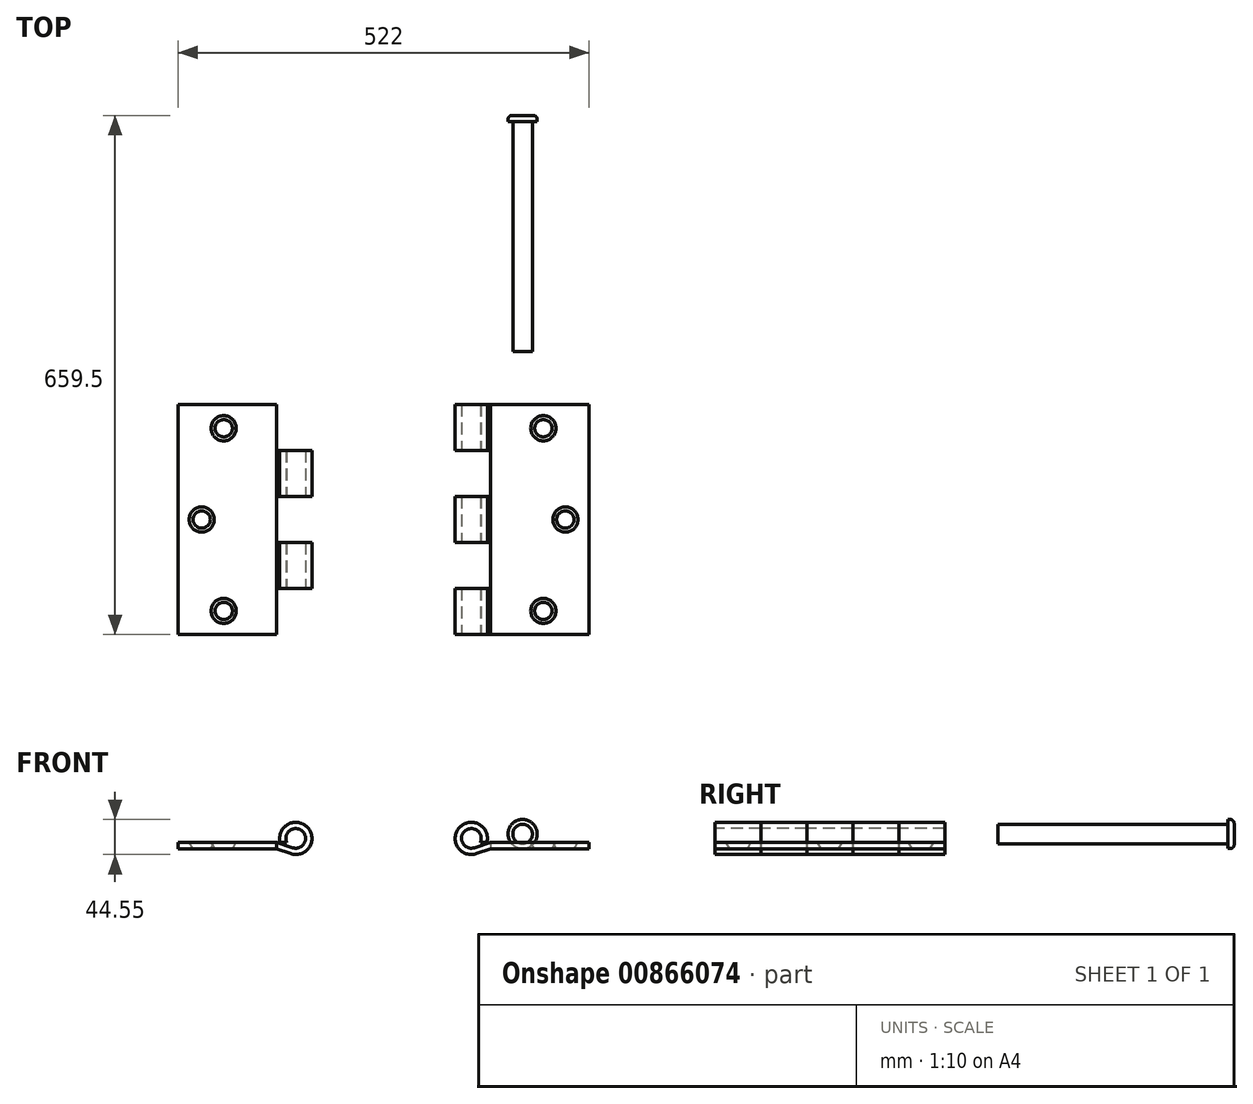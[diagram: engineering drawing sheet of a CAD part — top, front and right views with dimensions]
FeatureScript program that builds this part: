
annotation { "Feature Type Name" : "Feature", "Feature Type Description" : "" }
export const myFeature = defineFeature(function(context is Context, id is Id, definition is map)
    precondition{}
    {
        {
            var Q0;
            Q0=qCreatedBy(makeId("Top.planeOp"),FACE);
            var sketch = newSketch(context, id + "F0", { "sketchPlane" : qUnion([Q0])});
            skLineSegment(sketch, "E0.bottom", {"start": v(-62.5, 146) * mm, "end": v(62.5, 146) * mm});
            skLineSegment(sketch, "E0.top", {"start": v(-62.5, -146) * mm, "end": v(62.5, -146) * mm});
            skLineSegment(sketch, "E0.left", {"start": v(-62.5, 146) * mm, "end": v(-62.5, -146) * mm});
            skLineSegment(sketch, "E0.right", {"start": v(62.5, 146) * mm, "end": v(62.5, -146) * mm});
            skPoint(sketch, "E0.middle", {"position": v(0, 0) * mm});
            skSolve(sketch);
        }
        {
            var Q0;
            Q0=makeQuery(id+"F0.imprint","IMPRINT",FACE,{"disambiguationData":[TD([[makeQuery(id+"F0.imprint","IMPRINT",EDGE,{"derivedFrom":sQuery(id+"F0.wireOp",EDGE,"E0.bottom")}),-1.0]])]});
            extrude(context, id + "F1", {"entities" : qUnion([Q0]), "depth" : 8 * mm, "offsetDistance" : 25 * mm});
        }
        {
            var Q0;
            Q0=makeQuery(id+"F1.opExtrude","SWEPT_FACE",FACE,{"disambiguationData":[OSD([sQuery(id+"F0.wireOp",EDGE,"E0.top")])]});
            var sketch = newSketch(context, id + "F2", { "sketchPlane" : qUnion([Q0])});
            skArc(sketch, "E1", {"start": v(-67.12, 8) * mm, "mid": v(-102.19, 26.77) * mm, "end": v(-80.09, -6.3) * mm});
            skArc(sketch, "E2", {"start": v(-75.54, 8) * mm, "mid": v(-95.44, 22.22) * mm, "end": v(-83.04, 1.14) * mm});
            skLineSegment(sketch, "E3", {"start": v(-67.12, 8) * mm, "end": v(-75.54, 8) * mm});
            skLineSegment(sketch, "E4", {"start": v(-62.5, 0) * mm, "end": v(-80.09, -6.3) * mm});
            skLineSegment(sketch, "E5", {"start": v(-62.5, 8) * mm, "end": v(-83.04, 1.14) * mm});
            skSolve(sketch);
        }
        {
            var Q0;
            Q0=makeQuery(id+"F2.imprint","IMPRINT",FACE,{"disambiguationData":[TD([[makeQuery(id+"F2.imprint","IMPRINT",EDGE,{"derivedFrom":sQuery(id+"F2.wireOp",EDGE,"E1")}),1.0]])]});
            extrude(context, id + "F3", {"entities" : qUnion([Q0]), "operationType" : NewBodyOperationType.ADD, "oppositeDirection" : true, "depth" : 292 * mm, "offsetDistance" : 25 * mm});
        }
        {
            var Q0;
            Q0=makeQuery(id+"F1.opExtrude","CAP_FACE",FACE,{"disambiguationData":[OSD([sQuery(id+"F0.wireOp",EDGE,"E0.bottom"),sQuery(id+"F0.wireOp",EDGE,"E0.top"),sQuery(id+"F0.wireOp",EDGE,"E0.left"),sQuery(id+"F0.wireOp",EDGE,"E0.right")])],"isStart":false});
            var sketch = newSketch(context, id + "F4", { "sketchPlane" : qUnion([Q0])});
            skCircle(sketch, "E6", {"center": v(4.5, 116) * mm, "radius": 16 * mm});
            skCircle(sketch, "E7", {"center": v(32.5, 0) * mm, "radius": 16 * mm});
            skCircle(sketch, "E8", {"center": v(4.5, -116) * mm, "radius": 16 * mm});
            skSolve(sketch);
        }
        {
            var Q0;
            Q0=makeQuery(id+"F1.opExtrude","CAP_FACE",FACE,{"disambiguationData":[OSD([sQuery(id+"F0.wireOp",EDGE,"E0.bottom"),sQuery(id+"F0.wireOp",EDGE,"E0.top"),sQuery(id+"F0.wireOp",EDGE,"E0.left"),sQuery(id+"F0.wireOp",EDGE,"E0.right")])],"isStart":true});
            var sketch = newSketch(context, id + "F5", { "sketchPlane" : qUnion([Q0])});
            skPoint(sketch, "E9.0", {"position": v(32.5, 0) * mm});
            skPoint(sketch, "E10.0", {"position": v(4.5, 116) * mm});
            skPoint(sketch, "E11.0", {"position": v(4.5, -116) * mm});
            skCircle(sketch, "E12", {"center": v(32.5, 0) * mm, "radius": 11 * mm});
            skCircle(sketch, "E13", {"center": v(4.5, 116) * mm, "radius": 11 * mm});
            skCircle(sketch, "E14", {"center": v(4.5, -116) * mm, "radius": 11 * mm});
            skSolve(sketch);
        }
        {
            var Q1;
            Q1=makeQuery(id+"F4.imprint","IMPRINT",FACE,{"disambiguationData":[TD([[makeQuery(id+"F4.imprint","IMPRINT",EDGE,{"derivedFrom":sQuery(id+"F4.wireOp",EDGE,"E8")}),1.0]])]});
            var Q2;
            Q2=makeQuery(id+"F5.imprint","IMPRINT",FACE,{"disambiguationData":[TD([[makeQuery(id+"F5.imprint","IMPRINT",EDGE,{"derivedFrom":sQuery(id+"F5.wireOp",EDGE,"E13")}),1.0]])]});
            loft(context, id + "F6", {"operationType" : NewBodyOperationType.REMOVE, "sheetProfilesArray" : [{ "sheetProfileEntities" : qUnion([Q1]) }, { "sheetProfileEntities" : qUnion([Q2]) }]});
        }
        {
            var Q1;
            Q1=makeQuery(id+"F5.imprint","IMPRINT",FACE,{"disambiguationData":[TD([[makeQuery(id+"F5.imprint","IMPRINT",EDGE,{"derivedFrom":sQuery(id+"F5.wireOp",EDGE,"E12")}),1.0]])]});
            var Q2;
            Q2=makeQuery(id+"F4.imprint","IMPRINT",FACE,{"disambiguationData":[TD([[makeQuery(id+"F4.imprint","IMPRINT",EDGE,{"derivedFrom":sQuery(id+"F4.wireOp",EDGE,"E7")}),1.0]])]});
            loft(context, id + "F7", {"operationType" : NewBodyOperationType.REMOVE, "sheetProfilesArray" : [{ "sheetProfileEntities" : qUnion([Q1]) }, { "sheetProfileEntities" : qUnion([Q2]) }]});
        }
        {
            var Q1;
            Q1=makeQuery(id+"F4.imprint","IMPRINT",FACE,{"disambiguationData":[TD([[makeQuery(id+"F4.imprint","IMPRINT",EDGE,{"derivedFrom":sQuery(id+"F4.wireOp",EDGE,"E6")}),1.0]])]});
            var Q2;
            Q2=makeQuery(id+"F5.imprint","IMPRINT",FACE,{"disambiguationData":[TD([[makeQuery(id+"F5.imprint","IMPRINT",EDGE,{"derivedFrom":sQuery(id+"F5.wireOp",EDGE,"E14")}),1.0]])]});
            loft(context, id + "F8", {"operationType" : NewBodyOperationType.REMOVE, "sheetProfilesArray" : [{ "sheetProfileEntities" : qUnion([Q1]) }, { "sheetProfileEntities" : qUnion([Q2]) }]});
        }
        {
            var Q0;
            Q0=makeQuery(id+"F1.opExtrude","SWEPT_FACE",FACE,{"disambiguationData":[OSD([sQuery(id+"F0.wireOp",EDGE,"E0.right")])]});
            cPlane(context, id + "F9", {"entities" : qUnion([Q0]), "cplaneType" : CPlaneType.OFFSET, "offset" : 261 * mm, "oppositeDirection" : true, "width" : 150 * mm, "height" : 150 * mm});
        }
        {
            var Q0;
            Q0=makeQuery(id+"F1.opExtrude","SWEPT_BODY",BODY,{"disambiguationData":[OSD([sQuery(id+"F0.wireOp",EDGE,"E0.bottom"),sQuery(id+"F0.wireOp",EDGE,"E0.top"),sQuery(id+"F0.wireOp",EDGE,"E0.left"),sQuery(id+"F0.wireOp",EDGE,"E0.right")])]});
            var Q1;
            Q1=qCreatedBy(id+"F9.planeOp",FACE);
            mirror(context, id + "F10", {"entities" : qUnion([Q0]), "mirrorPlane" : qUnion([Q1])});
        }
        {
            var Q0;
            Q0=makeQuery(id+"F10.opPattern","COPY",FACE,{"derivedFrom":makeQuery(id+"F1.opExtrude","CAP_FACE",FACE,{"disambiguationData":[OSD([sQuery(id+"F0.wireOp",EDGE,"E0.bottom"),sQuery(id+"F0.wireOp",EDGE,"E0.top"),sQuery(id+"F0.wireOp",EDGE,"E0.left"),sQuery(id+"F0.wireOp",EDGE,"E0.right")])],"isStart":false}),"instanceName":"1"});
            var sketch = newSketch(context, id + "F11", { "sketchPlane" : qUnion([Q0])});
            skLineSegment(sketch, "E15.bottom", {"start": v(-334.5, -146) * mm, "end": v(-245.1, -146) * mm});
            skLineSegment(sketch, "E15.top", {"start": v(-334.5, -87.6) * mm, "end": v(-245.1, -87.6) * mm});
            skLineSegment(sketch, "E15.left", {"start": v(-334.5, -146) * mm, "end": v(-334.5, -87.6) * mm});
            skLineSegment(sketch, "E15.right", {"start": v(-245.1, -146) * mm, "end": v(-245.1, -87.6) * mm});
            skLineSegment(sketch, "E16.bottom", {"start": v(-334.5, -29.2) * mm, "end": v(-245.1, -29.2) * mm});
            skLineSegment(sketch, "E16.top", {"start": v(-334.5, 29.2) * mm, "end": v(-245.1, 29.2) * mm});
            skLineSegment(sketch, "E16.left", {"start": v(-334.5, -29.2) * mm, "end": v(-334.5, 29.2) * mm});
            skLineSegment(sketch, "E16.right", {"start": v(-245.1, -29.2) * mm, "end": v(-245.1, 29.2) * mm});
            skLineSegment(sketch, "E17.bottom", {"start": v(-334.5, 146) * mm, "end": v(-263.09, 146) * mm});
            skLineSegment(sketch, "E17.top", {"start": v(-334.5, 87.6) * mm, "end": v(-263.09, 87.6) * mm});
            skLineSegment(sketch, "E17.left", {"start": v(-334.5, 146) * mm, "end": v(-334.5, 87.6) * mm});
            skLineSegment(sketch, "E17.right", {"start": v(-263.09, 146) * mm, "end": v(-263.09, 87.6) * mm});
            skSolve(sketch);
        }
        {
            var Q0;
            Q0=makeQuery(id+"F4.imprint","IMPRINT",FACE,{"disambiguationData":[TD([[makeQuery(id+"F4.imprint","IMPRINT",EDGE,{"derivedFrom":sQuery(id+"F4.wireOp",EDGE,"E6")}),-1.0]])]});
            var sketch = newSketch(context, id + "F12", { "sketchPlane" : qUnion([Q0])});
            skPoint(sketch, "E18.0", {"position": v(-62.5, 146) * mm});
            skPoint(sketch, "E19.0", {"position": v(-62.5, -146) * mm});
            skLineSegment(sketch, "E20.0", {"start": v(-62.5, 146) * mm, "end": v(-62.5, -146) * mm});
            skLineSegment(sketch, "E21.bottom", {"start": v(-62.5, -87.61) * mm, "end": v(-139.25, -87.61) * mm});
            skLineSegment(sketch, "E21.top", {"start": v(-62.5, -29.2) * mm, "end": v(-139.25, -29.2) * mm});
            skLineSegment(sketch, "E21.left", {"start": v(-62.5, -87.61) * mm, "end": v(-62.5, -29.2) * mm});
            skLineSegment(sketch, "E21.right", {"start": v(-139.25, -87.61) * mm, "end": v(-139.25, -29.2) * mm});
            skLineSegment(sketch, "E22.bottom", {"start": v(-62.5, 87.6) * mm, "end": v(-139.25, 87.6) * mm});
            skLineSegment(sketch, "E22.top", {"start": v(-62.5, 29.2) * mm, "end": v(-139.25, 29.2) * mm});
            skLineSegment(sketch, "E22.left", {"start": v(-62.5, 87.6) * mm, "end": v(-62.5, 29.2) * mm});
            skLineSegment(sketch, "E22.right", {"start": v(-139.25, 87.6) * mm, "end": v(-139.25, 29.2) * mm});
            skSolve(sketch);
        }
        {
            var Q0;
            Q0=makeQuery(id+"F11.imprint","IMPRINT",FACE,{"disambiguationData":[TD([[makeQuery(id+"F11.imprint","IMPRINT",EDGE,{"derivedFrom":sQuery(id+"F11.wireOp",EDGE,"E17.bottom")}),-1.0]])]});
            var Q1;
            Q1=makeQuery(id+"F11.imprint","IMPRINT",FACE,{"disambiguationData":[TD([[makeQuery(id+"F11.imprint","IMPRINT",EDGE,{"derivedFrom":sQuery(id+"F11.wireOp",EDGE,"E16.bottom")}),1.0]])]});
            var Q2;
            Q2=makeQuery(id+"F11.imprint","IMPRINT",FACE,{"disambiguationData":[TD([[makeQuery(id+"F11.imprint","IMPRINT",EDGE,{"derivedFrom":sQuery(id+"F11.wireOp",EDGE,"E15.bottom")}),1.0]])]});
            var Q3;
            Q3=makeQuery(id+"F12.imprint","IMPRINT",FACE,{"disambiguationData":[TD([[makeQuery(id+"F12.imprint","IMPRINT",EDGE,{"derivedFrom":sQuery(id+"F12.wireOp",EDGE,"E21.bottom")}),-1.0]])]});
            var Q4;
            Q4=makeQuery(id+"F12.imprint","IMPRINT",FACE,{"disambiguationData":[TD([[makeQuery(id+"F12.imprint","IMPRINT",EDGE,{"derivedFrom":sQuery(id+"F12.wireOp",EDGE,"E22.bottom")}),1.0]])]});
            extrude(context, id + "F13", {"entities" : qUnion([Q0, Q1, Q2, Q3, Q4]), "operationType" : NewBodyOperationType.REMOVE, "endBound" : BoundingType.SYMMETRIC, "depth" : 100 * mm, "offsetDistance" : 25 * mm});
        }
        {
            var Q0;
            Q0=makeQuery(id+"F3.boolean.opBoolean","MERGE",FACE,{"derivedFrom":[makeQuery(id+"F1.opExtrude","SWEPT_FACE",FACE,{"disambiguationData":[OSD([sQuery(id+"F0.wireOp",EDGE,"E0.bottom")])]}),makeQuery(id+"F3.opExtrude","CAP_FACE",FACE,{"disambiguationData":[OSD([sQuery(id+"F0.wireOp",EDGE,"E0.top"),sQuery(id+"F0.wireOp",EDGE,"E0.left"),sQuery(id+"F2.wireOp",EDGE,"E1"),sQuery(id+"F2.wireOp",EDGE,"E2"),sQuery(id+"F2.wireOp",EDGE,"E3"),sQuery(id+"F2.wireOp",EDGE,"E4"),sQuery(id+"F2.wireOp",EDGE,"E5")])],"isStart":false})]});
            cPlane(context, id + "F14", {"entities" : qUnion([Q0]), "cplaneType" : CPlaneType.OFFSET, "offset" : 67.5 * mm, "width" : 150 * mm, "height" : 150 * mm});
        }
        {
            var Q0;
            Q0=qCreatedBy(id+"F14.planeOp",FACE);
            var sketch = newSketch(context, id + "F15", { "sketchPlane" : qUnion([Q0])});
            skCircle(sketch, "E23", {"center": v(21.82, 18.55) * mm, "radius": 12.5 * mm});
            skSolve(sketch);
        }
        {
            var Q0;
            Q0=makeQuery(id+"F15.imprint","IMPRINT",FACE,{"disambiguationData":[TD([[makeQuery(id+"F15.imprint","IMPRINT",EDGE,{"derivedFrom":sQuery(id+"F15.wireOp",EDGE,"E23")}),1.0]])]});
            extrude(context, id + "F16", {"entities" : qUnion([Q0]), "operationType" : NewBodyOperationType.ADD, "depth" : 292 * mm, "offsetDistance" : 25 * mm});
        }
        {
            var Q0;
            Q0=makeQuery(id+"F16.opExtrude","CAP_FACE",FACE,{"disambiguationData":[OSD([sQuery(id+"F15.wireOp",EDGE,"E23")])],"isStart":false});
            var sketch = newSketch(context, id + "F17", { "sketchPlane" : qUnion([Q0])});
            skCircle(sketch, "E24", {"center": v(21.82, 18.55) * mm, "radius": 18.5 * mm});
            skSolve(sketch);
        }
        {
            var Q0;
            Q0=makeQuery(id+"F17.imprint","IMPRINT",FACE,{"disambiguationData":[TD([[makeQuery(id+"F17.imprint","IMPRINT",EDGE,{"derivedFrom":makeQuery(id+"F16.opExtrude","CAP_EDGE",EDGE,{"disambiguationData":[OSD([sQuery(id+"F15.wireOp",EDGE,"E23")])],"isStart":false})}),1.0]])]});
            var Q1;
            Q1=makeQuery(id+"F17.imprint","IMPRINT",FACE,{"disambiguationData":[TD([[makeQuery(id+"F17.imprint","IMPRINT",EDGE,{"derivedFrom":sQuery(id+"F17.wireOp",EDGE,"E24")}),1.0]])]});
            extrude(context, id + "F18", {"entities" : qUnion([Q0, Q1]), "operationType" : NewBodyOperationType.ADD, "depth" : 8 * mm, "offsetDistance" : 25 * mm});
        }
        {
            var Q0;
            Q0=makeQuery(id+"F18.opExtrude","CAP_FACE",FACE,{"disambiguationData":[OSD([sQuery(id+"F17.wireOp",EDGE,"E24")])],"isStart":false});
            fillet(context, id + "F19", {"entities" : qUnion([Q0]), "radius" : 5 * mm, "tangentPropagation" : true, "allowEdgeOverflow" : false});
        }
    });
